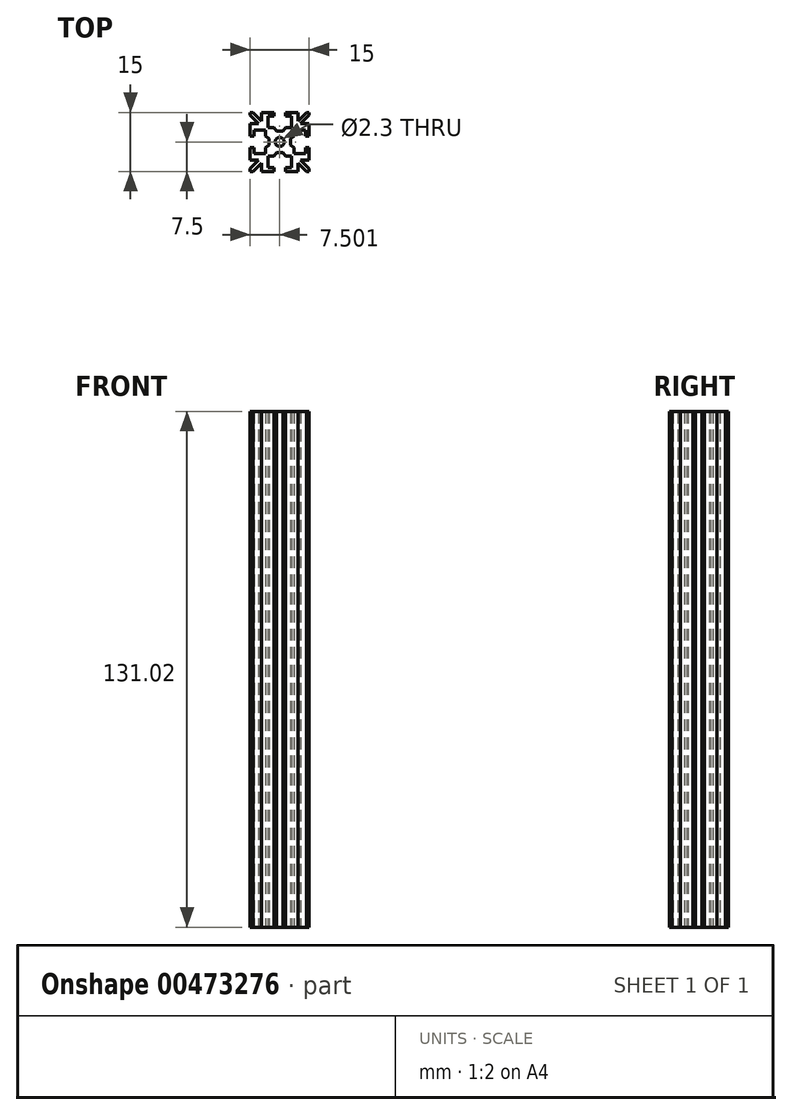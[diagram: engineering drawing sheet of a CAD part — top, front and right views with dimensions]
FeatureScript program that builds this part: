
annotation { "Feature Type Name" : "Feature", "Feature Type Description" : "" }
export const myFeature = defineFeature(function(context is Context, id is Id, definition is map)
    precondition{}
    {
        {
            var Q0;
            Q0=qCreatedBy(makeId("Top.planeOp"), FACE);
            var sketch = newSketch(context, id + "F0", { "sketchPlane" : qUnion([Q0])});
            skLineSegment(sketch, "E0", {"start": v(1.41, -1.6) * mm, "end": v(-6.09, -1.6) * mm, "construction": true});
            skLineSegment(sketch, "E1", {"start": v(-6.09, -0.1) * mm, "end": v(-6.09, 3.03) * mm});
            skLineSegment(sketch, "E2", {"start": v(1.41, 5.9) * mm, "end": v(1.41, -1.6) * mm, "construction": true});
            skArc(sketch, "E3", {"start": v(1.41, -0.45) * mm, "mid": v(0.6, -0.79) * mm, "end": v(0.26, -1.6) * mm});
            skLineSegment(sketch, "E4", {"start": v(1.41, -1.6) * mm, "end": v(-6.09, 5.9) * mm, "construction": true});
            skLineSegment(sketch, "E5.top", {"start": v(-6.09, -0.1) * mm, "end": v(-5.09, -0.1) * mm});
            skLineSegment(sketch, "E5.left", {"start": v(-6.09, 5.9) * mm, "end": v(-6.09, 5.2) * mm});
            skLineSegment(sketch, "E6", {"start": v(-5.09, -0.1) * mm, "end": v(-5.09, 1.4) * mm});
            skLineSegment(sketch, "E7", {"start": v(-5.09, 1.4) * mm, "end": v(-2.24, 1.4) * mm});
            skLineSegment(sketch, "E8", {"start": v(-2.24, 1.4) * mm, "end": v(-2.24, -0.1) * mm});
            skLineSegment(sketch, "E9", {"start": v(-2.24, -0.1) * mm, "end": v(-1.3, -0.79) * mm});
            skLineSegment(sketch, "E10", {"start": v(-1.3, -0.79) * mm, "end": v(-1.3, -1.6) * mm});
            skLineSegment(sketch, "E11", {"start": v(-6.09, 5.2) * mm, "end": v(-3.93, 3.03) * mm});
            skLineSegment(sketch, "E12", {"start": v(-3.93, 3.03) * mm, "end": v(-6.09, 3.03) * mm});
            skLineSegment(sketch, "E13.trimOffspring", {"start": v(-6.09, 3.03) * mm, "end": v(-6.09, -0.1) * mm});
            skLineSegment(sketch, "E14.trimOffspring", {"start": v(-6.09, 5.2) * mm, "end": v(-6.09, 5.9) * mm});
            skLineSegment(sketch, "E15.MirrorCS", {"start": v(-0.09, 5.9) * mm, "end": v(-3.22, 5.9) * mm});
            skLineSegment(sketch, "E16.MirrorCS", {"start": v(-6.09, 5.9) * mm, "end": v(-5.38, 5.9) * mm});
            skLineSegment(sketch, "E17.MirrorCS", {"start": v(-5.38, 5.9) * mm, "end": v(-6.09, 5.9) * mm});
            skLineSegment(sketch, "E18.MirrorCS", {"start": v(-3.22, 5.9) * mm, "end": v(-0.09, 5.9) * mm});
            skLineSegment(sketch, "E19.MirrorCS", {"start": v(-5.38, 5.9) * mm, "end": v(-3.22, 3.74) * mm});
            skLineSegment(sketch, "E20.MirrorCS", {"start": v(-1.59, 2.05) * mm, "end": v(-0.09, 2.05) * mm});
            skLineSegment(sketch, "E21.MirrorCS", {"start": v(-0.09, 2.05) * mm, "end": v(0.6, 1.11) * mm});
            skLineSegment(sketch, "E22.MirrorCS", {"start": v(-1.59, 4.9) * mm, "end": v(-1.59, 2.05) * mm});
            skLineSegment(sketch, "E23.MirrorCS", {"start": v(-0.09, 5.9) * mm, "end": v(-0.09, 4.9) * mm});
            skLineSegment(sketch, "E24.MirrorCS", {"start": v(-0.09, 4.9) * mm, "end": v(-1.59, 4.9) * mm});
            skLineSegment(sketch, "E25.MirrorCS", {"start": v(-3.22, 3.74) * mm, "end": v(-3.22, 5.9) * mm});
            skLineSegment(sketch, "E26.MirrorCS", {"start": v(0.6, 1.11) * mm, "end": v(1.41, 1.11) * mm});
            skLineSegment(sketch, "E27.MirrorCS", {"start": v(8.91, 3.03) * mm, "end": v(8.91, -0.1) * mm});
            skLineSegment(sketch, "E28.MirrorCS", {"start": v(8.91, 5.2) * mm, "end": v(8.91, 5.9) * mm});
            skLineSegment(sketch, "E29.MirrorCS", {"start": v(8.91, 5.9) * mm, "end": v(8.2, 5.9) * mm});
            skLineSegment(sketch, "E30.MirrorCS", {"start": v(6.04, 5.9) * mm, "end": v(2.91, 5.9) * mm});
            skLineSegment(sketch, "E31.MirrorCS", {"start": v(2.91, 5.9) * mm, "end": v(6.04, 5.9) * mm});
            skLineSegment(sketch, "E32.MirrorCS", {"start": v(8.2, 5.9) * mm, "end": v(8.91, 5.9) * mm});
            skLineSegment(sketch, "E33.MirrorCS", {"start": v(8.2, 5.9) * mm, "end": v(6.04, 3.74) * mm});
            skLineSegment(sketch, "E34.MirrorCS", {"start": v(2.91, 2.05) * mm, "end": v(2.23, 1.11) * mm});
            skLineSegment(sketch, "E35.MirrorCS", {"start": v(4.41, 4.9) * mm, "end": v(4.41, 2.05) * mm});
            skLineSegment(sketch, "E36.MirrorCS", {"start": v(2.91, 4.9) * mm, "end": v(4.41, 4.9) * mm});
            skLineSegment(sketch, "E37.MirrorCS", {"start": v(2.23, 1.11) * mm, "end": v(1.41, 1.11) * mm});
            skLineSegment(sketch, "E38.MirrorCS", {"start": v(8.91, 5.2) * mm, "end": v(6.75, 3.03) * mm});
            skLineSegment(sketch, "E39.MirrorCS", {"start": v(4.13, -0.79) * mm, "end": v(4.13, -1.6) * mm});
            skLineSegment(sketch, "E40.MirrorCS", {"start": v(5.06, -0.1) * mm, "end": v(4.13, -0.79) * mm});
            skLineSegment(sketch, "E41.MirrorCS", {"start": v(5.06, 1.4) * mm, "end": v(5.06, -0.1) * mm});
            skLineSegment(sketch, "E42.MirrorCS", {"start": v(7.91, 1.4) * mm, "end": v(5.06, 1.4) * mm});
            skLineSegment(sketch, "E43.MirrorCS", {"start": v(7.91, -0.1) * mm, "end": v(7.91, 1.4) * mm});
            skLineSegment(sketch, "E44.MirrorCS", {"start": v(8.91, 5.9) * mm, "end": v(8.91, 5.2) * mm});
            skLineSegment(sketch, "E45.MirrorCS", {"start": v(8.91, -0.1) * mm, "end": v(7.91, -0.1) * mm});
            skLineSegment(sketch, "E46.MirrorCS", {"start": v(1.41, -1.6) * mm, "end": v(8.91, 5.9) * mm, "construction": true});
            skLineSegment(sketch, "E47.MirrorCS", {"start": v(8.91, -0.1) * mm, "end": v(8.91, 3.03) * mm});
            skArc(sketch, "E48.MirrorCS", {"start": v(1.41, -0.45) * mm, "mid": v(2.22, -0.79) * mm, "end": v(2.56, -1.6) * mm});
            skLineSegment(sketch, "E49.MirrorCS", {"start": v(1.41, -1.6) * mm, "end": v(8.91, -1.6) * mm, "construction": true});
            skLineSegment(sketch, "E50.MirrorCS", {"start": v(6.75, 3.03) * mm, "end": v(8.91, 3.03) * mm});
            skLineSegment(sketch, "E51.MirrorCS", {"start": v(6.04, 3.74) * mm, "end": v(6.04, 5.9) * mm});
            skLineSegment(sketch, "E52.MirrorCS", {"start": v(2.91, 5.9) * mm, "end": v(2.91, 4.9) * mm});
            skLineSegment(sketch, "E53.MirrorCS", {"start": v(4.41, 2.05) * mm, "end": v(2.91, 2.05) * mm});
            skLineSegment(sketch, "E54.MirrorCS", {"start": v(-3.22, -9.1) * mm, "end": v(-0.09, -9.1) * mm});
            skLineSegment(sketch, "E55.MirrorCS", {"start": v(2.91, -5.25) * mm, "end": v(2.23, -4.31) * mm});
            skLineSegment(sketch, "E56.MirrorCS", {"start": v(-6.09, -6.23) * mm, "end": v(-6.09, -3.1) * mm});
            skLineSegment(sketch, "E57.MirrorCS", {"start": v(-6.09, -8.4) * mm, "end": v(-6.09, -9.1) * mm});
            skLineSegment(sketch, "E58.MirrorCS", {"start": v(8.91, -9.1) * mm, "end": v(8.91, -8.4) * mm});
            skLineSegment(sketch, "E59.MirrorCS", {"start": v(-6.09, -9.1) * mm, "end": v(-5.38, -9.1) * mm});
            skLineSegment(sketch, "E60.MirrorCS", {"start": v(8.91, -9.1) * mm, "end": v(8.2, -9.1) * mm});
            skLineSegment(sketch, "E61.MirrorCS", {"start": v(2.91, -9.1) * mm, "end": v(6.04, -9.1) * mm});
            skLineSegment(sketch, "E62.MirrorCS", {"start": v(8.91, -3.1) * mm, "end": v(8.91, -6.23) * mm});
            skLineSegment(sketch, "E63.MirrorCS", {"start": v(5.06, -4.6) * mm, "end": v(5.06, -3.1) * mm});
            skLineSegment(sketch, "E64.MirrorCS", {"start": v(-3.22, -6.94) * mm, "end": v(-3.22, -9.1) * mm});
            skLineSegment(sketch, "E65.MirrorCS", {"start": v(6.75, -6.23) * mm, "end": v(8.91, -6.23) * mm});
            skLineSegment(sketch, "E66.MirrorCS", {"start": v(-3.93, -6.23) * mm, "end": v(-6.09, -6.23) * mm});
            skLineSegment(sketch, "E67.MirrorCS", {"start": v(-6.09, -3.1) * mm, "end": v(-6.09, -6.23) * mm});
            skLineSegment(sketch, "E68.MirrorCS", {"start": v(1.41, -9.1) * mm, "end": v(1.41, -1.6) * mm, "construction": true});
            skArc(sketch, "E69.MirrorCS", {"start": v(1.41, -2.75) * mm, "mid": v(0.6, -2.41) * mm, "end": v(0.26, -1.6) * mm});
            skLineSegment(sketch, "E70.MirrorCS", {"start": v(1.41, -1.6) * mm, "end": v(-6.09, -9.1) * mm, "construction": true});
            skLineSegment(sketch, "E71.MirrorCS", {"start": v(-6.09, -3.1) * mm, "end": v(-5.09, -3.1) * mm});
            skLineSegment(sketch, "E72.MirrorCS", {"start": v(-6.09, -9.1) * mm, "end": v(-6.09, -8.4) * mm});
            skLineSegment(sketch, "E73.MirrorCS", {"start": v(-5.09, -3.1) * mm, "end": v(-5.09, -4.6) * mm});
            skLineSegment(sketch, "E74.MirrorCS", {"start": v(-5.09, -4.6) * mm, "end": v(-2.24, -4.6) * mm});
            skLineSegment(sketch, "E75.MirrorCS", {"start": v(-2.24, -4.6) * mm, "end": v(-2.24, -3.1) * mm});
            skLineSegment(sketch, "E76.MirrorCS", {"start": v(-2.24, -3.1) * mm, "end": v(-1.3, -2.41) * mm});
            skLineSegment(sketch, "E77.MirrorCS", {"start": v(-1.3, -2.41) * mm, "end": v(-1.3, -1.6) * mm});
            skLineSegment(sketch, "E78.MirrorCS", {"start": v(-6.09, -8.4) * mm, "end": v(-3.93, -6.23) * mm});
            skLineSegment(sketch, "E79.MirrorCS", {"start": v(7.91, -4.6) * mm, "end": v(5.06, -4.6) * mm});
            skLineSegment(sketch, "E80.MirrorCS", {"start": v(0.6, -4.31) * mm, "end": v(1.41, -4.31) * mm});
            skLineSegment(sketch, "E81.MirrorCS", {"start": v(8.91, -8.4) * mm, "end": v(6.75, -6.23) * mm});
            skLineSegment(sketch, "E82.MirrorCS", {"start": v(-1.59, -8.1) * mm, "end": v(-1.59, -5.25) * mm});
            skLineSegment(sketch, "E83.MirrorCS", {"start": v(-5.38, -9.1) * mm, "end": v(-3.22, -6.94) * mm});
            skLineSegment(sketch, "E84.MirrorCS", {"start": v(6.04, -6.94) * mm, "end": v(6.04, -9.1) * mm});
            skLineSegment(sketch, "E85.MirrorCS", {"start": v(8.91, -8.4) * mm, "end": v(8.91, -9.1) * mm});
            skLineSegment(sketch, "E86.MirrorCS", {"start": v(4.41, -8.1) * mm, "end": v(4.41, -5.25) * mm});
            skLineSegment(sketch, "E87.MirrorCS", {"start": v(-0.09, -9.1) * mm, "end": v(-3.22, -9.1) * mm});
            skLineSegment(sketch, "E88.MirrorCS", {"start": v(8.2, -9.1) * mm, "end": v(6.04, -6.94) * mm});
            skLineSegment(sketch, "E89.MirrorCS", {"start": v(8.2, -9.1) * mm, "end": v(8.91, -9.1) * mm});
            skLineSegment(sketch, "E90.MirrorCS", {"start": v(1.41, -1.6) * mm, "end": v(8.91, -9.1) * mm, "construction": true});
            skArc(sketch, "E91.MirrorCS", {"start": v(1.41, -2.75) * mm, "mid": v(2.22, -2.41) * mm, "end": v(2.56, -1.6) * mm});
            skLineSegment(sketch, "E92.MirrorCS", {"start": v(2.91, -8.1) * mm, "end": v(4.41, -8.1) * mm});
            skLineSegment(sketch, "E93.MirrorCS", {"start": v(8.91, -3.1) * mm, "end": v(7.91, -3.1) * mm});
            skLineSegment(sketch, "E94.MirrorCS", {"start": v(2.91, -9.1) * mm, "end": v(2.91, -8.1) * mm});
            skLineSegment(sketch, "E95.MirrorCS", {"start": v(-1.59, -5.25) * mm, "end": v(-0.09, -5.25) * mm});
            skLineSegment(sketch, "E96.MirrorCS", {"start": v(-0.09, -9.1) * mm, "end": v(-0.09, -8.1) * mm});
            skLineSegment(sketch, "E97.MirrorCS", {"start": v(4.13, -2.41) * mm, "end": v(4.13, -1.6) * mm});
            skLineSegment(sketch, "E98.MirrorCS", {"start": v(8.91, -6.23) * mm, "end": v(8.91, -3.1) * mm});
            skLineSegment(sketch, "E99.MirrorCS", {"start": v(7.91, -3.1) * mm, "end": v(7.91, -4.6) * mm});
            skLineSegment(sketch, "E100.MirrorCS", {"start": v(-5.38, -9.1) * mm, "end": v(-6.09, -9.1) * mm});
            skLineSegment(sketch, "E101.MirrorCS", {"start": v(4.41, -5.25) * mm, "end": v(2.91, -5.25) * mm});
            skLineSegment(sketch, "E102.MirrorCS", {"start": v(6.04, -9.1) * mm, "end": v(2.91, -9.1) * mm});
            skLineSegment(sketch, "E103.MirrorCS", {"start": v(-0.09, -8.1) * mm, "end": v(-1.59, -8.1) * mm});
            skLineSegment(sketch, "E104.MirrorCS", {"start": v(5.06, -3.1) * mm, "end": v(4.13, -2.41) * mm});
            skLineSegment(sketch, "E105.MirrorCS", {"start": v(2.23, -4.31) * mm, "end": v(1.41, -4.31) * mm});
            skLineSegment(sketch, "E106.MirrorCS", {"start": v(-0.09, -5.25) * mm, "end": v(0.6, -4.31) * mm});
            skSolve(sketch);
        }
        {
            var Q0;
            Q0 = qSketchRegion(id + "F0", true);
            extrude(context, id + "F1", {"entities" : qUnion([Q0]), "depth" : 131.02 * mm, "offsetDistance" : 25 * mm});
        }
    });
